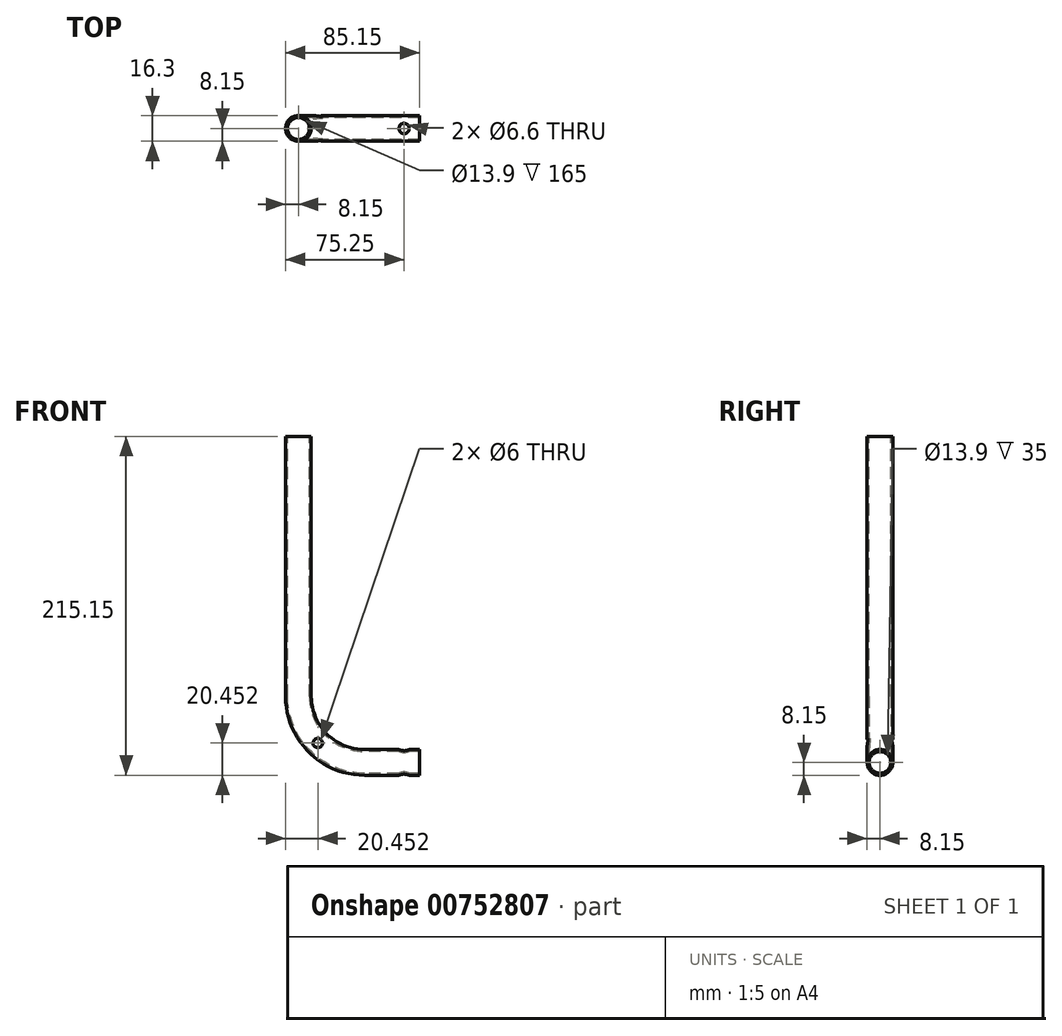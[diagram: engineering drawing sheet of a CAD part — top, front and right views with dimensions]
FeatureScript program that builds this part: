
annotation { "Feature Type Name" : "Feature", "Feature Type Description" : "" }
export const myFeature = defineFeature(function(context is Context, id is Id, definition is map)
    precondition{}
    {
        {
            var Q0;
            Q0=qCreatedBy(makeId("Front.planeOp"),FACE);
            var sketch = newSketch(context, id + "F0", { "sketchPlane" : qUnion([Q0])});
            skLineSegment(sketch, "E0", {"start": v(-77, 207) * mm, "end": v(-77, 42) * mm});
            skArc(sketch, "E1", {"start": v(-77, 42) * mm, "mid": v(-64.7, 12.3) * mm, "end": v(-35, 0) * mm});
            skLineSegment(sketch, "E2", {"start": v(-35, 0) * mm, "end": v(0, 0) * mm});
            skSolve(sketch);
        }
        {
            var Q0;
            Q0=qCreatedBy(makeId("Right.planeOp"),FACE);
            var sketch = newSketch(context, id + "F1", { "sketchPlane" : qUnion([Q0])});
            skCircle(sketch, "E3", {"center": v(0, 0) * mm, "radius": 8.15 * mm});
            skCircle(sketch, "E4.0", {"center": v(0, 0) * mm, "radius": 6.95 * mm});
            skSolve(sketch);
        }
        {
            var Q0;
            Q0=makeQuery(id+"F1.imprint","IMPRINT",FACE,{"disambiguationData":[TD([[makeQuery(id+"F1.imprint","IMPRINT",EDGE,{"derivedFrom":sQuery(id+"F1.wireOp",EDGE,"E3")}),1.0]])]});
            var Q1;
            Q1=sQuery(id+"F0.wireOp",EDGE,"E2");
            var Q2;
            Q2=sQuery(id+"F0.wireOp",EDGE,"E1");
            var Q3;
            Q3=sQuery(id+"F0.wireOp",EDGE,"E0");
            sweep(context, id + "F2", {"profiles" : qUnion([Q0]), "path" : qUnion([Q1, Q2, Q3])});
        }
        {
            var Q0;
            Q0=qCreatedBy(makeId("Front.planeOp"),FACE);
            var sketch = newSketch(context, id + "F3", { "sketchPlane" : qUnion([Q0])});
            skArc(sketch, "E5", {"start": v(-35, 8.15) * mm, "mid": v(-58.94, 18.06) * mm, "end": v(-68.85, 42) * mm, "construction": true});
            skArc(sketch, "E6", {"start": v(-85.15, 42) * mm, "mid": v(-70.46, 6.54) * mm, "end": v(-35, -8.15) * mm, "construction": true});
            skLineSegment(sketch, "E7", {"start": v(-58.94, 18.06) * mm, "end": v(-70.46, 6.54) * mm, "construction": true});
            skCircle(sketch, "E8", {"center": v(-64.7, 12.3) * mm, "radius": 3 * mm});
            skSolve(sketch);
        }
        {
            var Q0;
            Q0=makeQuery(id+"F3.imprint","IMPRINT",FACE,{"disambiguationData":[TD([[makeQuery(id+"F3.imprint","IMPRINT",EDGE,{"derivedFrom":sQuery(id+"F3.wireOp",EDGE,"E8")}),1.0]])]});
            extrude(context, id + "F4", {"entities" : qUnion([Q0]), "operationType" : NewBodyOperationType.REMOVE, "oppositeDirection" : true, "depth" : 25 * mm, "offsetDistance" : 25 * mm, "symmetric" : true});
        }
        {
            var Q0;
            Q0=qCreatedBy(makeId("Top.planeOp"),FACE);
            var sketch = newSketch(context, id + "F5", { "sketchPlane" : qUnion([Q0])});
            skLineSegment(sketch, "E9", {"start": v(-35, -8.15) * mm, "end": v(0, -8.15) * mm, "construction": true});
            skLineSegment(sketch, "E10", {"start": v(0, 8.15) * mm, "end": v(-35, 8.15) * mm, "construction": true});
            skLineSegment(sketch, "E11", {"start": v(-9.9, -8.15) * mm, "end": v(-9.9, 8.15) * mm, "construction": true});
            skCircle(sketch, "E12", {"center": v(-9.9, 0) * mm, "radius": 3.3 * mm});
            skSolve(sketch);
        }
        {
            var Q0;
            Q0 = qSketchRegion(id + "F5", true);
            extrude(context, id + "F6", {"entities" : qUnion([Q0]), "operationType" : NewBodyOperationType.REMOVE, "oppositeDirection" : true, "depth" : 25 * mm, "offsetDistance" : 25 * mm, "symmetric" : true});
        }
    });
